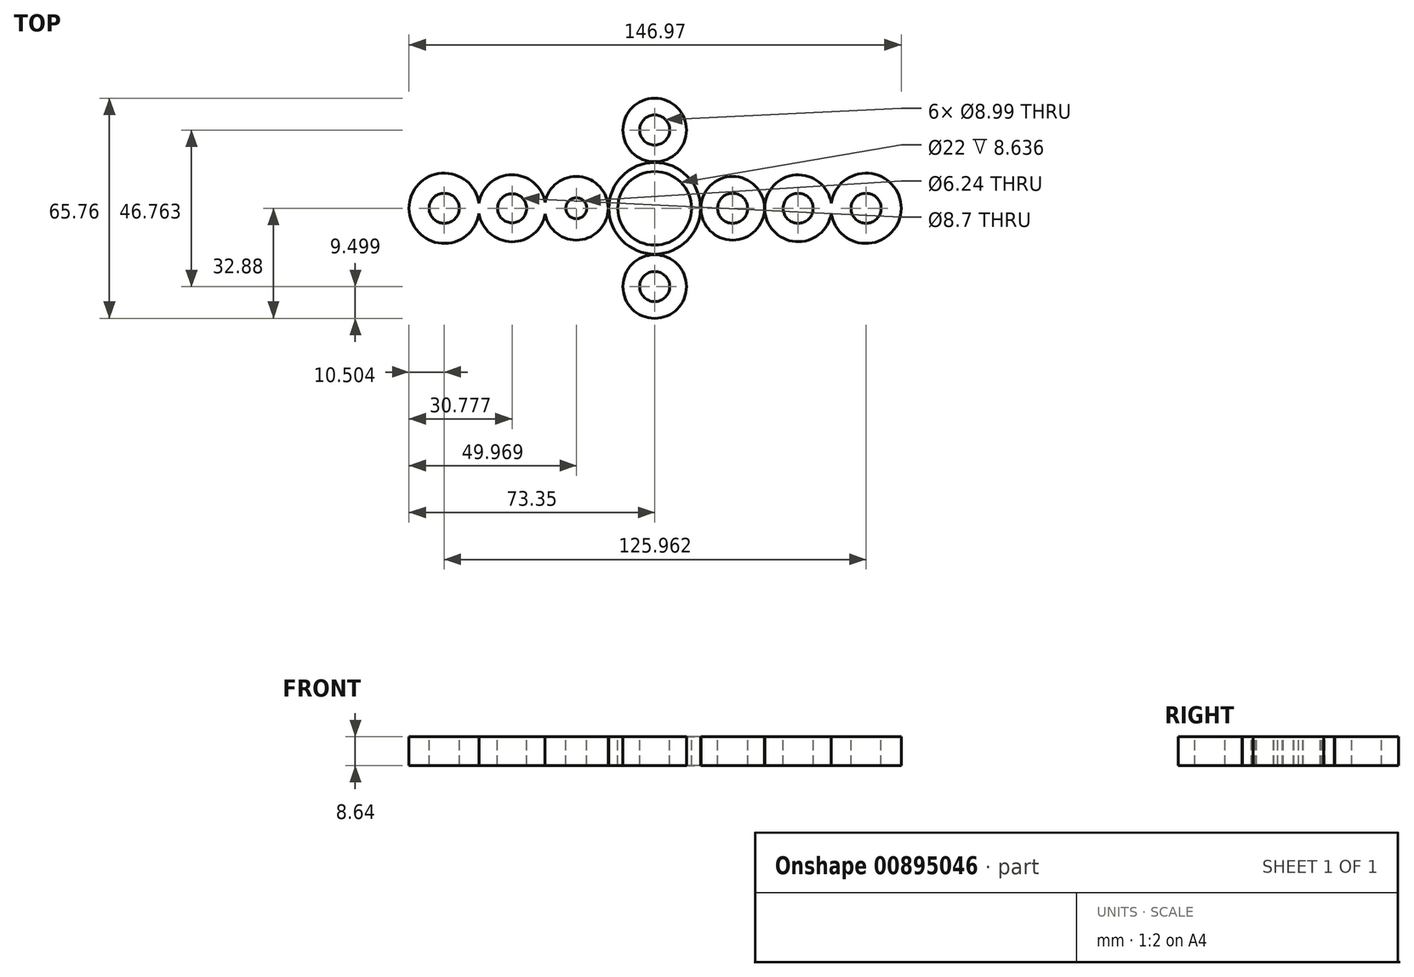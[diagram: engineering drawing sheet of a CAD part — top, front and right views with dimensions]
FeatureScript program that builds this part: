
annotation { "Feature Type Name" : "Feature", "Feature Type Description" : "" }
export const myFeature = defineFeature(function(context is Context, id is Id, definition is map)
    precondition{}
    {
        {
            var Q0;
            Q0=qCreatedBy(makeId("Top.planeOp"),FACE);
            var sketch = newSketch(context, id + "F0", { "sketchPlane" : qUnion([Q0])});
            skCircle(sketch, "E0", {"center": v(0, 0) * mm, "radius": 11 * mm});
            skCircle(sketch, "E1", {"center": v(0, 0) * mm, "radius": 13.68 * mm});
            skCircle(sketch, "E2", {"center": v(23.28, 0) * mm, "radius": 9.5 * mm});
            skCircle(sketch, "E3", {"center": v(-23.38, 0) * mm, "radius": 9.5 * mm});
            skCircle(sketch, "E4", {"center": v(0, 23.38) * mm, "radius": 9.5 * mm});
            skCircle(sketch, "E5", {"center": v(0, -23.38) * mm, "radius": 9.5 * mm});
            skCircle(sketch, "E6", {"center": v(-42.57, 0) * mm, "radius": 10 * mm});
            skCircle(sketch, "E7", {"center": v(42.84, 0) * mm, "radius": 10 * mm});
            skCircle(sketch, "E8", {"center": v(-62.85, 0) * mm, "radius": 10.5 * mm});
            skCircle(sketch, "E9", {"center": v(63.12, 0) * mm, "radius": 10.5 * mm});
            skCircle(sketch, "E10", {"center": v(-62.85, 0) * mm, "radius": 4.5 * mm});
            skCircle(sketch, "E11", {"center": v(-42.57, 0) * mm, "radius": 4.35 * mm});
            skCircle(sketch, "E12", {"center": v(-23.38, 0) * mm, "radius": 3.12 * mm});
            skCircle(sketch, "E13", {"center": v(23.28, 0) * mm, "radius": 4.5 * mm});
            skCircle(sketch, "E14", {"center": v(42.84, 0) * mm, "radius": 4.5 * mm});
            skCircle(sketch, "E15", {"center": v(63.12, 0) * mm, "radius": 4.5 * mm});
            skCircle(sketch, "E16", {"center": v(0, -23.38) * mm, "radius": 4.5 * mm});
            skCircle(sketch, "E17", {"center": v(0, 23.38) * mm, "radius": 4.5 * mm});
            skSolve(sketch);
        }
        {
            var Q0;
            Q0 = qSketchRegion(id + "F0", true);
            extrude(context, id + "F1", {"entities" : qUnion([Q0]), "oppositeDirection" : true, "depth" : 8.64 * mm, "offsetDistance" : 25.4 * mm});
        }
    });
